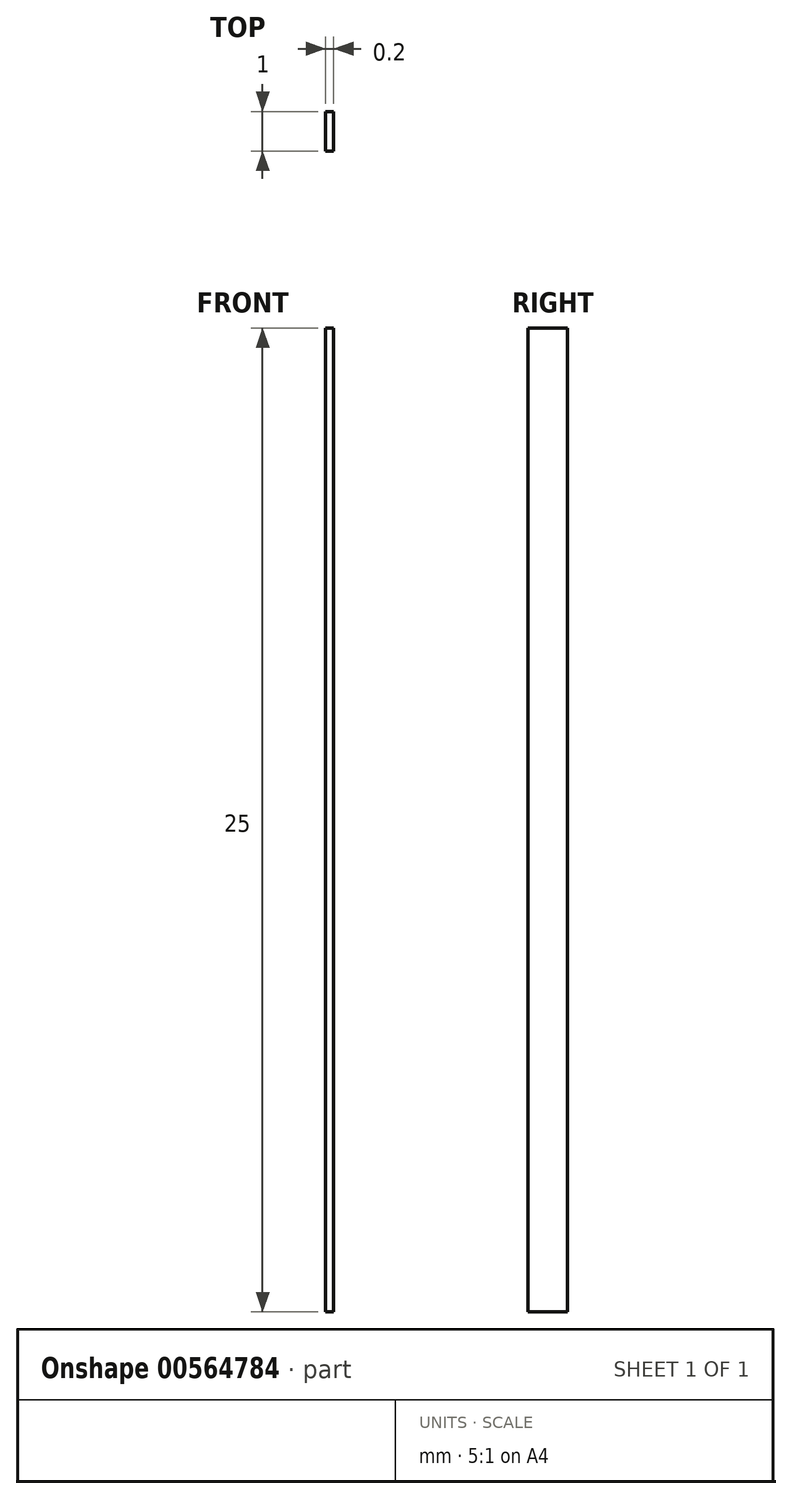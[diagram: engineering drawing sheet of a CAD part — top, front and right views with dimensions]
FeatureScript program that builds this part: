
annotation { "Feature Type Name" : "Feature", "Feature Type Description" : "" }
export const myFeature = defineFeature(function(context is Context, id is Id, definition is map)
    precondition{}
    {
        {
            var Q0;
            Q0=qCreatedBy(makeId("Top.planeOp"),FACE);
            var sketch = newSketch(context, id + "F0", { "sketchPlane" : qUnion([Q0])});
            skLineSegment(sketch, "E0.bottom", {"start": v(-0.1, -0.5) * mm, "end": v(0.1, -0.5) * mm});
            skLineSegment(sketch, "E0.top", {"start": v(-0.1, 0.5) * mm, "end": v(0.1, 0.5) * mm});
            skLineSegment(sketch, "E0.left", {"start": v(-0.1, -0.5) * mm, "end": v(-0.1, 0.5) * mm});
            skLineSegment(sketch, "E0.right", {"start": v(0.1, -0.5) * mm, "end": v(0.1, 0.5) * mm});
            skPoint(sketch, "E0.middle", {"position": v(0, 0) * mm});
            skSolve(sketch);
        }
        {
            var Q0;
            Q0 = qSketchRegion(id + "F0", true);
            extrude(context, id + "F1", {"entities" : qUnion([Q0]), "depth" : 25 * mm, "offsetDistance" : 25 * mm});
        }
    });
